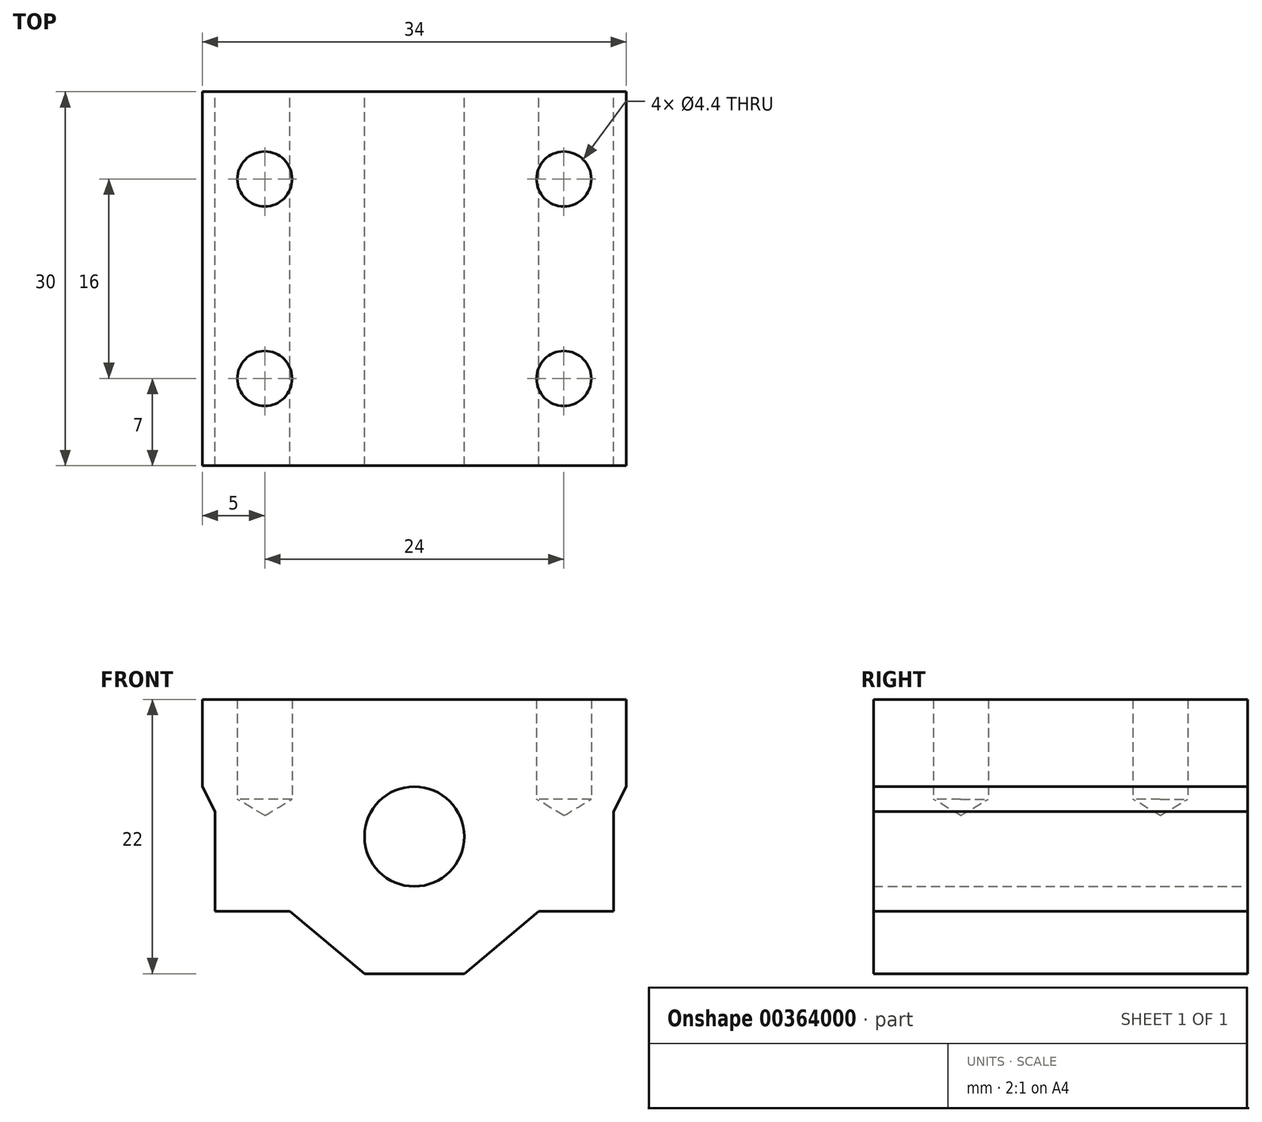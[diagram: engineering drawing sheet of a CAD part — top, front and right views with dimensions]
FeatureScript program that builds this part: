
annotation { "Feature Type Name" : "Feature", "Feature Type Description" : "" }
export const myFeature = defineFeature(function(context is Context, id is Id, definition is map)
    precondition{}
    {
        {
            var Q0;
            Q0=qCreatedBy(makeId("Front.planeOp"),FACE);
            var sketch = newSketch(context, id + "F0", { "sketchPlane" : qUnion([Q0])});
            skArc(sketch, "E0", {"start": v(0, 4) * mm, "mid": v(4, 0) * mm, "end": v(0, -4) * mm});
            skLineSegment(sketch, "E1", {"start": v(0, 11) * mm, "end": v(17, 11) * mm});
            skLineSegment(sketch, "E2", {"start": v(16, -6) * mm, "end": v(10, -6) * mm});
            skLineSegment(sketch, "E3", {"start": v(10, -6) * mm, "end": v(4, -11) * mm});
            skLineSegment(sketch, "E4", {"start": v(4, -11) * mm, "end": v(0, -11) * mm});
            skLineSegment(sketch, "E5", {"start": v(16, -6) * mm, "end": v(16, 2) * mm});
            skLineSegment(sketch, "E6", {"start": v(17, 11) * mm, "end": v(17, 4) * mm});
            skLineSegment(sketch, "E7", {"start": v(17, 4) * mm, "end": v(16, 2) * mm});
            skLineSegment(sketch, "E8.MirrorCS", {"start": v(-17, 4) * mm, "end": v(-16, 2) * mm});
            skLineSegment(sketch, "E9.MirrorCS", {"start": v(0, 11) * mm, "end": v(-17, 11) * mm});
            skLineSegment(sketch, "E10.MirrorCS", {"start": v(-4, -11) * mm, "end": v(0, -11) * mm});
            skLineSegment(sketch, "E11.MirrorCS", {"start": v(-17, 11) * mm, "end": v(-17, 4) * mm});
            skLineSegment(sketch, "E12.MirrorCS", {"start": v(-16, -6) * mm, "end": v(-16, 2) * mm});
            skLineSegment(sketch, "E13.MirrorCS", {"start": v(-16, -6) * mm, "end": v(-10, -6) * mm});
            skLineSegment(sketch, "E14.MirrorCS", {"start": v(-10, -6) * mm, "end": v(-4, -11) * mm});
            skArc(sketch, "E15.MirrorCS", {"start": v(0, 4) * mm, "mid": v(-4, 0) * mm, "end": v(0, -4) * mm});
            skSolve(sketch);
        }
        {
            var Q0;
            Q0 = qSketchRegion(id + "F0", true);
            extrude(context, id + "F1", {"entities" : qUnion([Q0]), "depth" : 30 * mm, "offsetDistance" : 25 * mm});
        }
        {
            var Q0;
            Q0=makeQuery(id+"F1.opExtrude","SWEPT_FACE",FACE,{"disambiguationData":[OSD([sQuery(id+"F0.wireOp",EDGE,"E1"),sQuery(id+"F0.wireOp",EDGE,"E9.MirrorCS")])]});
            var sketch = newSketch(context, id + "F2", { "sketchPlane" : qUnion([Q0])});
            skPoint(sketch, "E16", {"position": v(12, -7) * mm});
            skPoint(sketch, "E17.0.1.0", {"position": v(12, -23) * mm});
            skPoint(sketch, "E17.0.2.0", {"position": v(12, -39) * mm});
            skPoint(sketch, "E17.1.0.0", {"position": v(-12, -7) * mm});
            skPoint(sketch, "E17.1.1.0", {"position": v(-12, -23) * mm});
            skPoint(sketch, "E17.1.2.0", {"position": v(-12, -39) * mm});
            skLineSegment(sketch, "E17.direction1", {"start": v(12, -7) * mm, "end": v(-12, -7) * mm, "construction": true});
            skLineSegment(sketch, "E17.direction2", {"start": v(12, -7) * mm, "end": v(12, -23) * mm, "construction": true});
            skSolve(sketch);
        }
        {
            var Q0;
            Q0=sQuery(id+"F2.wireOp",VERTEX,"E17.1.1.0");
            var Q1;
            Q1=sQuery(id+"F2.wireOp",VERTEX,"E17.1.0.0");
            var Q2;
            Q2=sQuery(id+"F2.wireOp",VERTEX,"E16");
            var Q3;
            Q3=sQuery(id+"F2.wireOp",VERTEX,"E17.0.1.0");
            var Q4;
            Q4=makeQuery(id+"F1.opExtrude","SWEPT_BODY",BODY,{"disambiguationData":[OSD([sQuery(id+"F0.wireOp",EDGE,"E0"),sQuery(id+"F0.wireOp",EDGE,"E1"),sQuery(id+"F0.wireOp",EDGE,"E2"),sQuery(id+"F0.wireOp",EDGE,"E3"),sQuery(id+"F0.wireOp",EDGE,"E4"),sQuery(id+"F0.wireOp",EDGE,"E5"),sQuery(id+"F0.wireOp",EDGE,"E6"),sQuery(id+"F0.wireOp",EDGE,"E7"),sQuery(id+"F0.wireOp",EDGE,"E8.MirrorCS"),sQuery(id+"F0.wireOp",EDGE,"E9.MirrorCS"),sQuery(id+"F0.wireOp",EDGE,"E10.MirrorCS"),sQuery(id+"F0.wireOp",EDGE,"E11.MirrorCS"),sQuery(id+"F0.wireOp",EDGE,"E12.MirrorCS"),sQuery(id+"F0.wireOp",EDGE,"E13.MirrorCS"),sQuery(id+"F0.wireOp",EDGE,"E14.MirrorCS"),sQuery(id+"F0.wireOp",EDGE,"E15.MirrorCS")])]});
            hole(context, id + "F3", {"style" : HoleStyle.SIMPLE, "endStyle" : HoleEndStyle.BLIND, "standardTappedOrClearance" : lookupTablePath({ "standard" : "ISO", "fit" : "Normal", "size" : "M4", "type" : "Clearance" }), "standardBlindInLast" : lookupTablePath({ "fit" : "Standard", "standard" : "ISO", "size" : "M4", "type" : "Clearance" }), "holeDiameter" : 4.4 * mm, "majorDiameter" : 5 * mm, "holeDepth" : 8 * mm, "isTappedThrough" : true, "tappedDepth" : 12 * mm, "tapClearance" : 3, "locations" : qUnion([Q0, Q1, Q2, Q3]), "scope" : qUnion([Q4]), "startStyle" : HoleStartStyle.PART});
        }
    });
